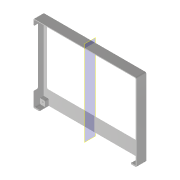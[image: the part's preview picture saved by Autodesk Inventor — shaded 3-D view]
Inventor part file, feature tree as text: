
AUTODESK INVENTOR PART (.ipt)
format: ipt  version: 2022 (Build 260153000, 153)  size: 257,024 bytes
history: native  units: mm
features: other x5, sketch x2, extrude x2, reference x2, pattern_linear x1, plane x1
ambient origin geometry x8: Origin, YZ Plane, XZ Plane, XY Plane, X Axis, Y Axis, Z Axis, Center Point
bodies: Volumenkörper1 (feature_tree)
feature tree (13):
  other  "40_ZTable_7Inch_Display_Housing_Lid"
  sketch  "Skizze1"  dims[d0=3.2mm d1=10.0mm]
  other  "Arbeitspunkt1"
  extrude  "Extrusion1"  Depth=10.0mm
  extrude  "Extrusion2"  Depth=4.0mm
  pattern_linear  "Rechteckige Anordnung1"  Spacing1=169.0mm  [1 undecoded]
  plane  "Arbeitsebene1"
  reference  "Referenz1"
  reference  "Referenz2"
  sketch  "Skizze2"  dims[d3=5.0mm d4=4.0mm d5=169.0mm d6=0.0mm d7=25.0mm d8=169.0mm d9=0.0mm d10=50.0mm d12=40.0mm]
  other  "MeshFeature1"
  other  "Assembly_7inch_Display.iam"
  other  "40_ZTable_7Inch_Display_Housing_Bottom:1"
note: 1 required parameter value undecoded (feature->parameter linkage not recoverable at this tier; creation-order binding heuristic only, values carry confidence <= 0.55)
